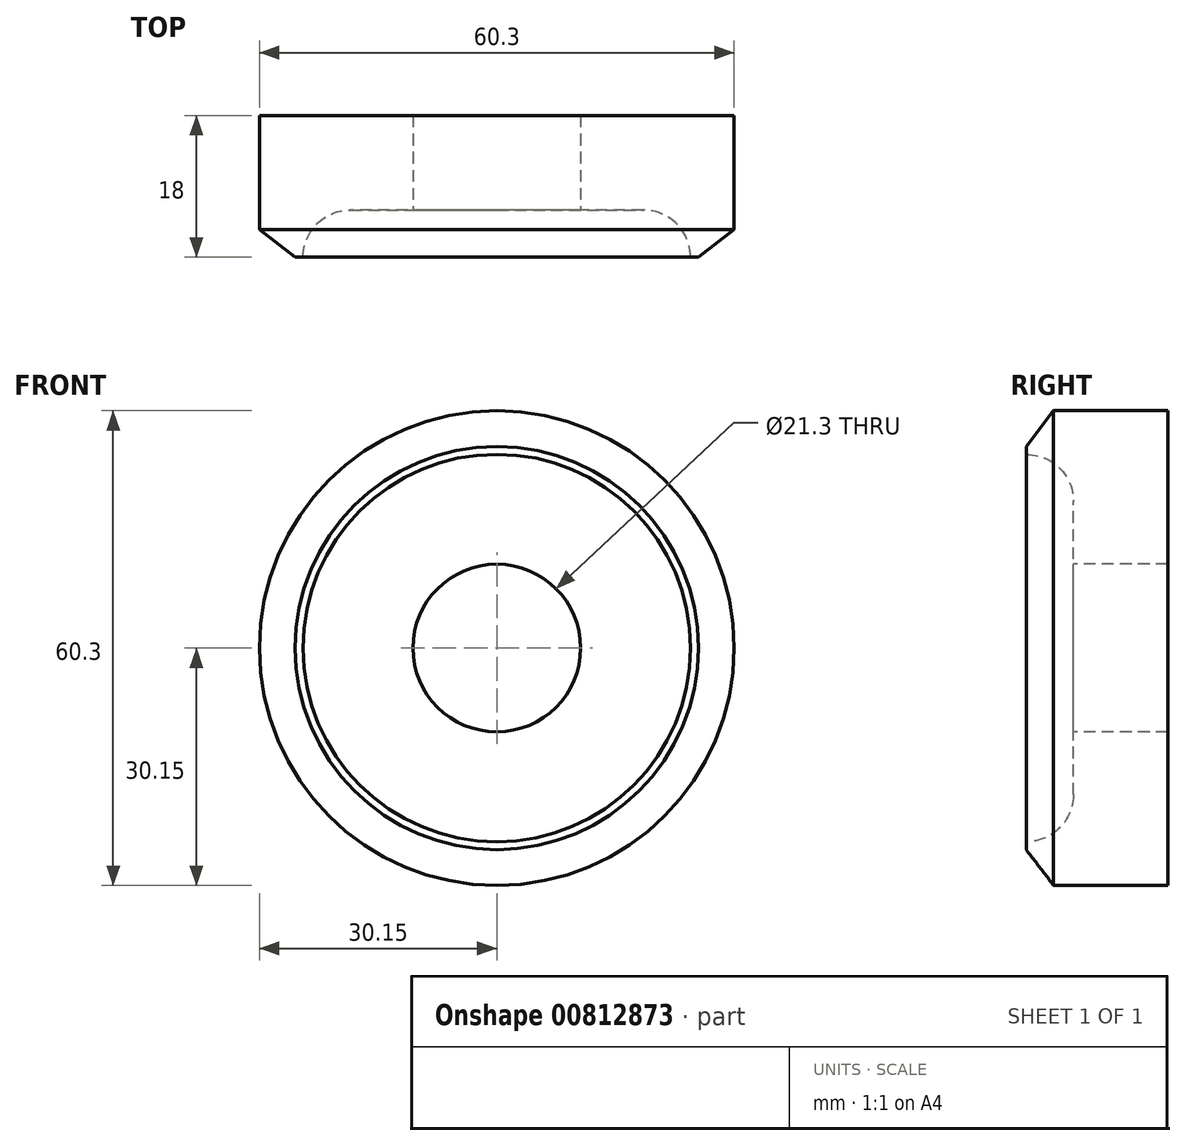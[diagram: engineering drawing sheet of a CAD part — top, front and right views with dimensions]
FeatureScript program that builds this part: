
annotation { "Feature Type Name" : "Feature", "Feature Type Description" : "" }
export const myFeature = defineFeature(function(context is Context, id is Id, definition is map)
    precondition{}
    {
        {
            var Q0;
            Q0=qCreatedBy(makeId("Front.planeOp"),FACE);
            var sketch = newSketch(context, id + "F0", { "sketchPlane" : qUnion([Q0])});
            skCircle(sketch, "E0", {"center": v(0, 0) * mm, "radius": 30.15 * mm});
            skSolve(sketch);
        }
        {
            var Q0;
            Q0 = qSketchRegion(id + "F0", true);
            extrude(context, id + "F1", {"entities" : qUnion([Q0]), "depth" : 18 * mm, "offsetDistance" : 25 * mm});
        }
        {
            var Q0;
            Q0=makeQuery(id+"F1.opExtrude","CAP_FACE",FACE,{"disambiguationData":[OSD([sQuery(id+"F0.wireOp",EDGE,"E0")])],"isStart":false});
            var sketch = newSketch(context, id + "F2", { "sketchPlane" : qUnion([Q0])});
            skSolve(sketch);
        }
        {
            var Q0;
            Q0=makeQuery(id+"F2.imprint","IMPRINT",FACE,{"disambiguationData":[TD([[makeQuery(id+"F2.imprint","IMPRINT",EDGE,{"derivedFrom":makeQuery(id+"F1.opExtrude","CAP_EDGE",EDGE,{"disambiguationData":[OSD([sQuery(id+"F0.wireOp",EDGE,"E0")])],"isStart":false})}),1.0]])]});
            var sketch = newSketch(context, id + "F3", { "sketchPlane" : qUnion([Q0])});
            skCircle(sketch, "E1", {"center": v(0, 0) * mm, "radius": 24.6 * mm});
            skSolve(sketch);
        }
        {
            var Q0;
            Q0 = qSketchRegion(id + "F3", true);
            extrude(context, id + "F4", {"entities" : qUnion([Q0]), "operationType" : NewBodyOperationType.REMOVE, "oppositeDirection" : true, "depth" : 6 * mm, "offsetDistance" : 25 * mm});
        }
        {
            var Q0;
            Q0=makeQuery(id+"F4.boolean.opBoolean","COPY",EDGE,{"derivedFrom":makeQuery(id+"F4.opExtrude","CAP_EDGE",EDGE,{"disambiguationData":[OSD([sQuery(id+"F3.wireOp",EDGE,"E1")])],"isStart":false})});
            fillet(context, id + "F5", {"entities" : qUnion([Q0]), "radius" : 6 * mm, "tangentPropagation" : true, "allowEdgeOverflow" : false});
        }
        {
            var Q0;
            Q0=makeQuery(id+"F2.imprint","IMPRINT",FACE,{"disambiguationData":[TD([[makeQuery(id+"F2.imprint","IMPRINT",EDGE,{"derivedFrom":makeQuery(id+"F1.opExtrude","CAP_EDGE",EDGE,{"disambiguationData":[OSD([sQuery(id+"F0.wireOp",EDGE,"E0")])],"isStart":false})}),1.0]])]});
            var sketch = newSketch(context, id + "F6", { "sketchPlane" : qUnion([Q0])});
            skCircle(sketch, "E2", {"center": v(0, 0) * mm, "radius": 10.65 * mm});
            skSolve(sketch);
        }
        {
            var Q0;
            Q0 = qSketchRegion(id + "F6", true);
            extrude(context, id + "F7", {"entities" : qUnion([Q0]), "operationType" : NewBodyOperationType.REMOVE, "oppositeDirection" : true, "depth" : 25 * mm, "offsetDistance" : 25 * mm});
        }
        {
            var Q0;
            Q0=qCreatedBy(makeId("Top.planeOp"),FACE);
            var sketch = newSketch(context, id + "F8", { "sketchPlane" : qUnion([Q0])});
            skLineSegment(sketch, "E3", {"start": v(-25.6, -18) * mm, "end": v(-30.15, -14.52) * mm});
            skLineSegment(sketch, "E4", {"start": v(-30.15, -14.52) * mm, "end": v(-30.15, -18.15) * mm});
            skLineSegment(sketch, "E5", {"start": v(-30.15, -18.15) * mm, "end": v(-25.6, -18) * mm});
            skLineSegment(sketch, "E6", {"start": v(0, 0) * mm, "end": v(0, -6.76) * mm});
            skSolve(sketch);
        }
        {
            var Q0;
            Q0 = qSketchRegion(id + "F8", true);
            var Q1;
            Q1=sQuery(id+"F8.wireOp",EDGE,"E6");
            revolve(context, id + "F9", {"operationType" : NewBodyOperationType.REMOVE, "surfaceOperationType" : NewSurfaceOperationType.NEW, "entities" : qUnion([Q0]), "axis" : qUnion([Q1]), "revolveType" : RevolveType.FULL, "oppositeDirection" : true});
        }
    });
